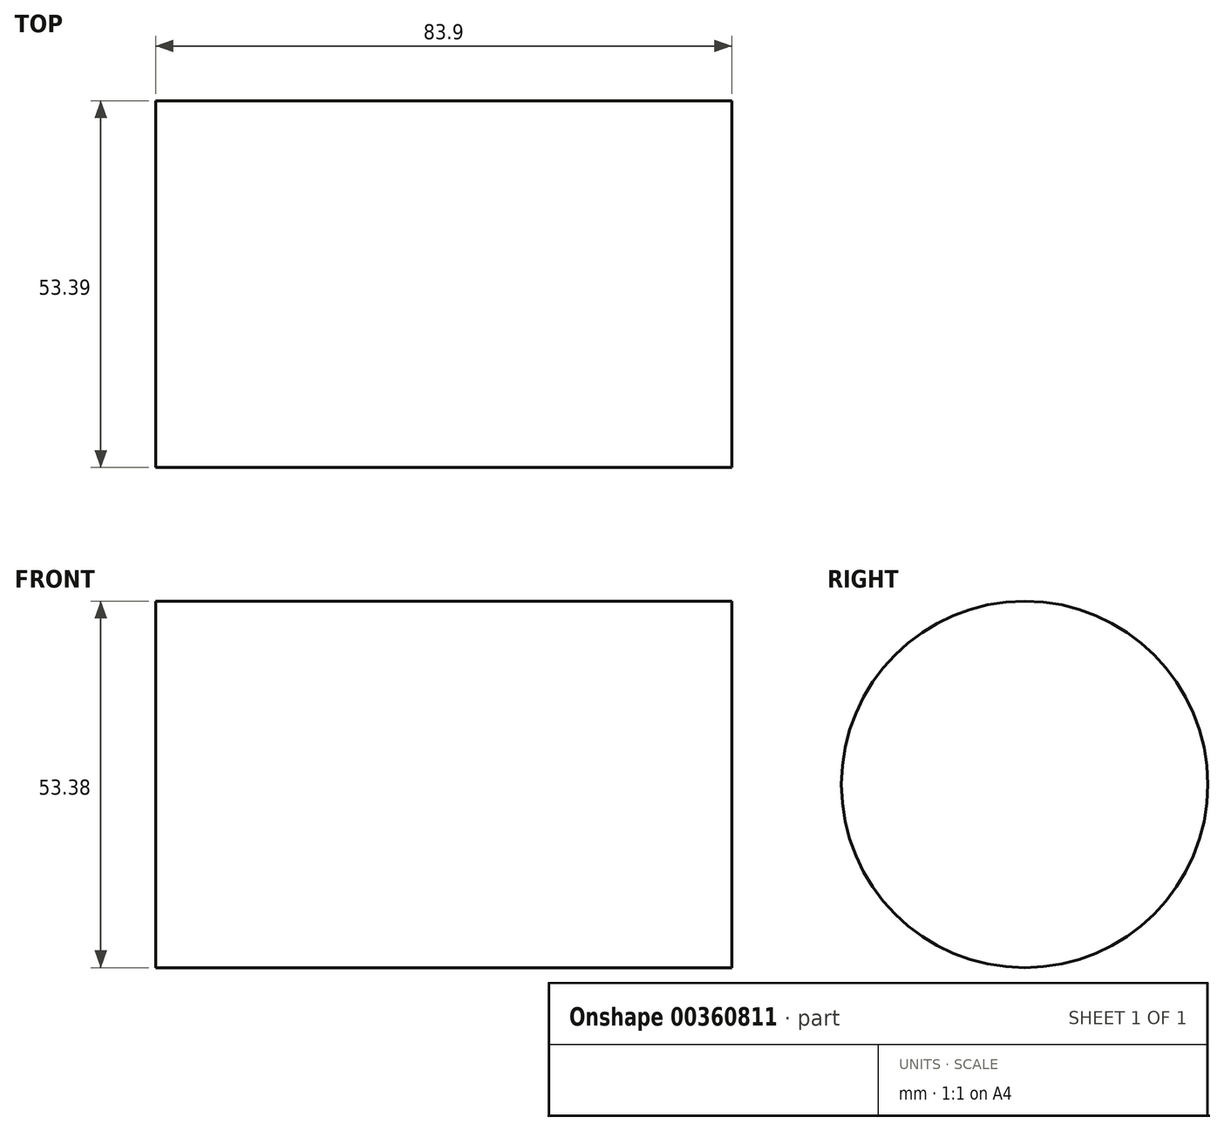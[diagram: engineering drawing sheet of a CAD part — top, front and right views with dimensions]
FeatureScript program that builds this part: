
annotation { "Feature Type Name" : "Feature", "Feature Type Description" : "" }
export const myFeature = defineFeature(function(context is Context, id is Id, definition is map)
    precondition{}
    {
        {
            var Q0;
            Q0=qCreatedBy(makeId("Right.planeOp"),FACE);
            var sketch = newSketch(context, id + "F0", { "sketchPlane" : qUnion([Q0])});
            skCircle(sketch, "E0", {"center": v(-94.59, 0) * mm, "radius": 1.98 * mm});
            skCircle(sketch, "E1", {"center": v(-145.34, 58.32) * mm, "radius": 26.7 * mm});
            skPoint(sketch, "E1.first.point", {"position": v(-134.34, 34) * mm});
            skPoint(sketch, "E1.second.point", {"position": v(-168.25, 72.01) * mm});
            skPoint(sketch, "E1.third.point", {"position": v(-171.76, 54.47) * mm});
            skCircle(sketch, "E2", {"center": v(-129.68, 64.66) * mm, "radius": 46.42 * mm});
            skPoint(sketch, "E2.first.point", {"position": v(-148.11, 22.06) * mm});
            skPoint(sketch, "E2.second.point", {"position": v(-144.2, 20.57) * mm});
            skPoint(sketch, "E2.third.point", {"position": v(-116.85, 109.27) * mm});
            skSolve(sketch);
        }
        {
            var Q0;
            Q0=makeQuery(id+"F0.imprint","IMPRINT",FACE,{"disambiguationData":[TD([[makeQuery(id+"F0.imprint","IMPRINT",EDGE,{"derivedFrom":sQuery(id+"F0.wireOp",EDGE,"E1")}),1.0]])]});
            extrude(context, id + "F1", {"entities" : qUnion([Q0]), "depth" : 71.2 * mm, "hasSecondDirection" : true, "secondDirectionOppositeDirection" : true, "secondDirectionDepth" : 12.7 * mm});
        }
    });
